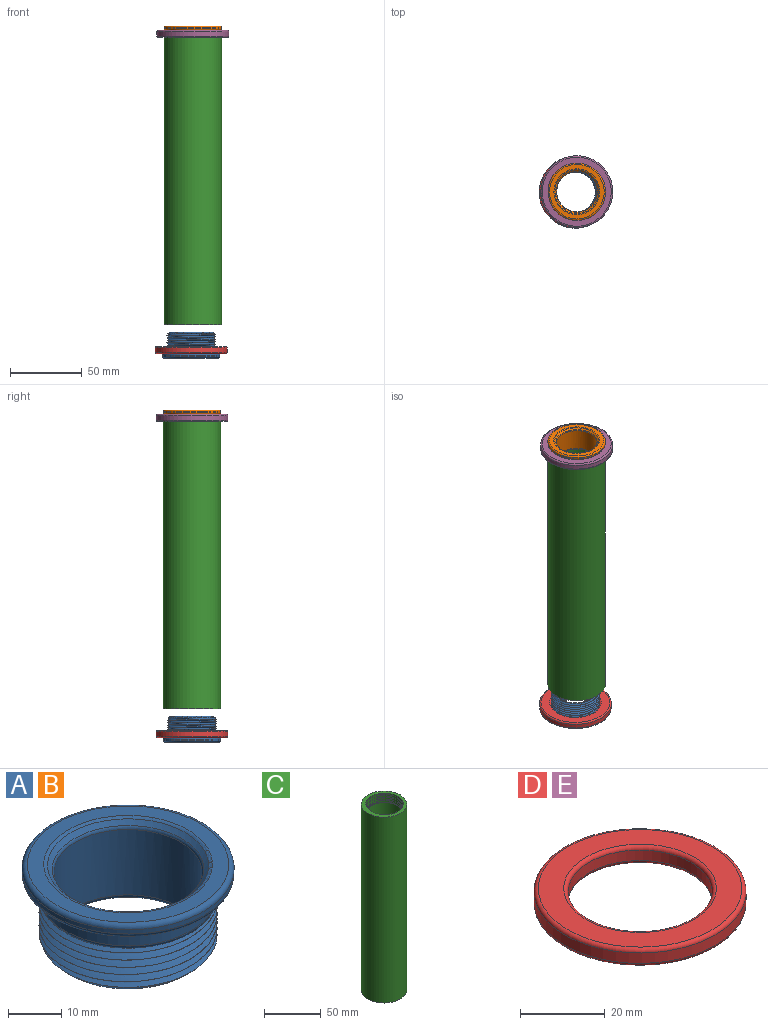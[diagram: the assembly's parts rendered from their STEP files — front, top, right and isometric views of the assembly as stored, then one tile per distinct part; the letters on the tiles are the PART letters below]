
ASSEMBLY  parts=5 mates=4
PART A: 18 faces, bbox 44.1x44.1x19.6 mm
  f0: plane 22.16x5mm, normal (0,0,-1), area 3.2mm2, adj f9,f16
  f1: cylinder r=20mm len=40mm, axis (0,0,-1), area 125.7mm2, adj f10,f11
  f2: cylinder r=14mm len=28mm, axis (0,0,-1), area 1327mm2, adj f8,f17
  f3: plane 38x38mm, normal (0,0,1), area 338.5mm2, adj f7,f11
  f4: plane 38x38mm, normal (0,0,-1), area 247.4mm2, adj f5,f10
  f5: cylinder r=16.8mm len=33.6mm, axis (0,0,1), area 422.2mm2, adj f4,f9
  f6: cone r=14mm half-angle=45deg, axis (0,0,1), area 119.8mm2, adj f7,f8
  f7: torus R=15.91mm, axis (0,0,1), area 76.7mm2, adj f3,f6
  f8: torus R=15mm, axis (0,0,-1), area 69.6mm2, adj f2,f6
  f9: torus R=15.8mm, axis (0,0,1), area 162.2mm2, adj f0,f5,f14
  f10: torus R=19mm, axis (0,0,1), area 193.8mm2, adj f1,f4
  f11: torus R=19mm, axis (0,0,1), area 193.8mm2, adj f1,f3
  f12: cylinder r=16.8mm len=33.6mm, axis (0,0,1), area 6.9mm2, adj f14,f15,f16
  f13: plane 30.6x30.6mm, normal (0,0,-1), area 28.6mm2, adj f15,f17
  f14: plane 33.2x29.27mm, normal (0,0,1), area 43.4mm2, adj f9,f12,f16
  f15: cone r=16.8mm half-angle=45deg, axis (0,0,1), area 123.3mm2, adj f12,f13,f16
  f16: bspline ~38.8x33.6mm, area 1646.9mm2, adj f0,f12,f14,f15
  f17: torus R=15mm, axis (0,0,1), area 141.8mm2, adj f2,f13
PART B: same geometry as A
PART C: 22 faces, bbox 40x40x203.3 mm
  f0: bspline ~39.26x34mm, area 1832mm2, adj f1,f2,f3,f4,f5,f6,f7,f17
  f1: cylinder r=17mm len=1.16mm, axis (0,0,-1), area 0mm2, adj f0,f2,f17
  f2: cylinder r=17mm len=34mm, axis (0,0,-1), area 1.8mm2, adj f0,f1,f3
  f3: cylinder r=17mm len=34mm, axis (0,0,-1), area 1.7mm2, adj f0,f2,f4
  f4: cylinder r=17mm len=34mm, axis (0,0,-1), area 1.8mm2, adj f0,f3,f5
  f5: cylinder r=17mm len=34mm, axis (0,0,-1), area 1.8mm2, adj f0,f4,f6
  f6: cylinder r=17mm len=34mm, axis (0,0,-1), area 1.7mm2, adj f0,f5,f7
  f7: cylinder r=17mm len=178.35mm, axis (0,0,-1), area 18783.3mm2, adj f0,f6,f8,f18,f19,f21
  f8: cylinder r=17mm len=34mm, axis (0,0,-1), area 1.8mm2, adj f7,f9,f19
  f9: cylinder r=17mm len=34mm, axis (0,0,-1), area 1.7mm2, adj f8,f10,f19
  f10: cylinder r=17mm len=34mm, axis (0,0,-1), area 1.9mm2, adj f9,f11,f19
  f11: cylinder r=17mm len=34mm, axis (0,0,-1), area 1.8mm2, adj f10,f12,f19
  f12: cylinder r=17mm len=34mm, axis (0,0,-1), area 1.8mm2, adj f11,f13,f19
  f13: cylinder r=17mm len=34mm, axis (0,0,-1), area 1.7mm2, adj f12,f14,f19
  f14: cylinder r=17mm len=34mm, axis (0,0,-1), area 1.8mm2, adj f13,f15,f19
  f15: cylinder r=17mm len=34mm, axis (0,0,-1), area 1.8mm2, adj f14,f19,f20
  f16: cylinder r=20mm len=200mm, axis (0,0,-1), area 25132.7mm2, adj f17,f20
  f17: plane 40x40mm, normal (0,0,1), area 411.4mm2, adj f0,f1,f16
  f18: plane 34x34mm, normal (0,0,-1), area 62.8mm2, adj f0,f7
  f19: bspline ~39.26x34mm, area 2596.8mm2, adj f7,f8,f9,f10,f11,f12,f13,f14
  f20: plane 40x40mm, normal (0,0,-1), area 411.4mm2, adj f15,f16,f19
  f21: plane 1.65x1.28mm, normal (0,1,0), area 1mm2, adj f7,f19
PART D: 8 faces, bbox 54.1x54.1x5 mm
  f0: cylinder r=17mm len=34mm, axis (0,0,-1), area 320.4mm2, adj f4,f6
  f1: cylinder r=25mm len=50mm, axis (0,0,-1), area 471.2mm2, adj f5,f7
  f2: plane 48x48mm, normal (0,0,1), area 791.7mm2, adj f6,f7
  f3: plane 48x48mm, normal (0,0,-1), area 791.7mm2, adj f4,f5
  f4: torus R=18mm, axis (0,0,1), area 171.4mm2, adj f0,f3
  f5: torus R=24mm, axis (0,0,1), area 243.2mm2, adj f1,f3
  f6: torus R=18mm, axis (0,0,1), area 171.4mm2, adj f0,f2
  f7: torus R=24mm, axis (0,0,1), area 243.2mm2, adj f1,f2
PART E: same geometry as D
PLACE A rot(axis=(1,0,0),180deg) t=(-1.17,0.04,-20)mm
PLACE B rot(axis=(0,0,-1),90deg) t=(0,0,205)mm
PLACE C at identity fixed
PLACE D t=(-1.17,0.04,-20)mm
PLACE E rot(axis=(0,0,-1),90deg) t=(0,0,200)mm
MATE slider E.f1 <-> C.f16  axis (0,0,-1) through (0,0,200)mm
MATE slider D.f1 <-> C.f20  axis (0,0,1) through (-1.17,0.04,-15)mm
MATE fastened A.f5 <-> D.f1  axis (0,0,1) through (-1.17,0.04,-20)mm
MATE fastened B.f5 <-> E.f1  axis (0,0,-1) through (0,0,205)mm
